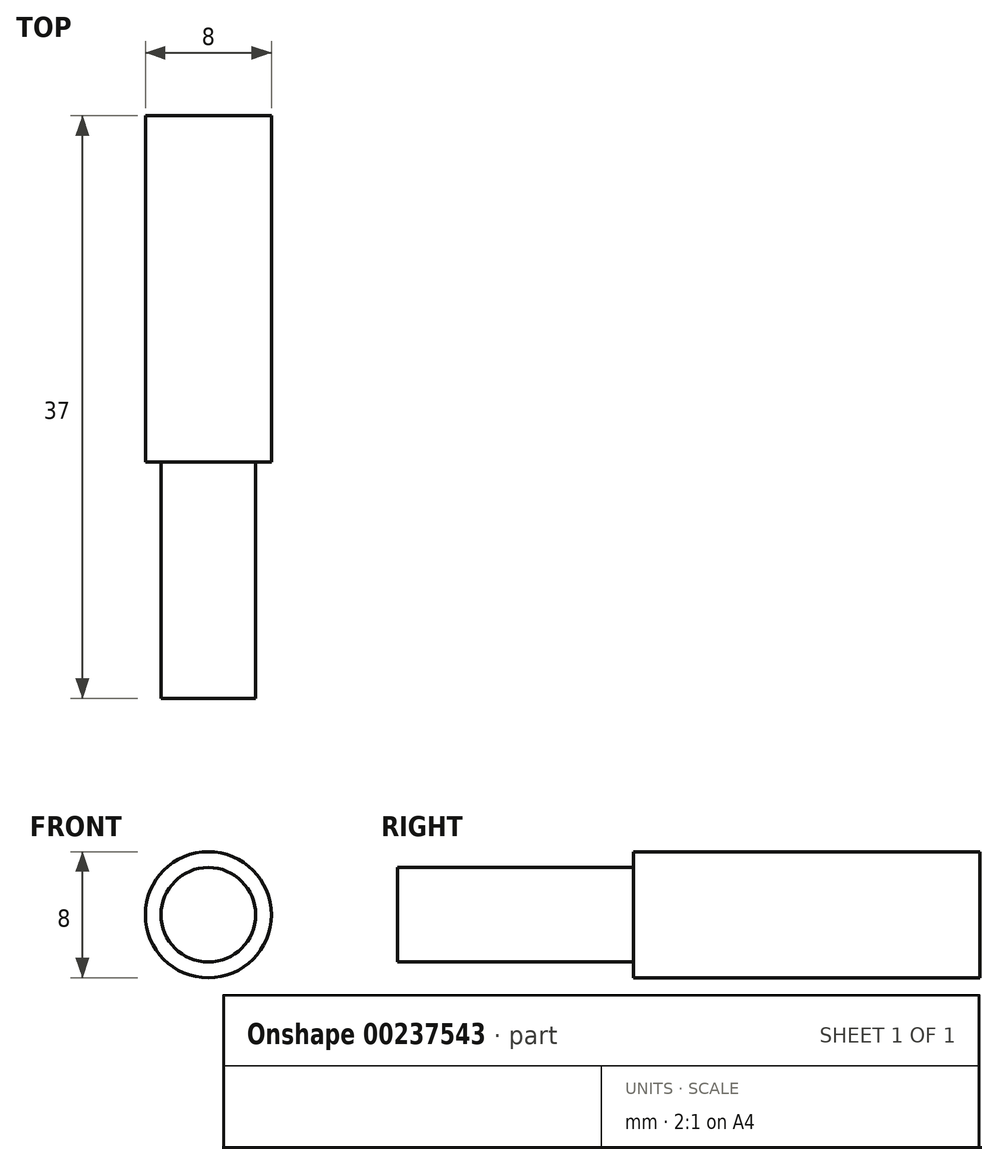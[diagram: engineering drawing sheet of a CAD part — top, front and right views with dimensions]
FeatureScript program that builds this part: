
annotation { "Feature Type Name" : "Feature", "Feature Type Description" : "" }
export const myFeature = defineFeature(function(context is Context, id is Id, definition is map)
    precondition{}
    {
        {
            var Q0;
            Q0=qCreatedBy(makeId("Right.planeOp"),FACE);
            var sketch = newSketch(context, id + "F0", { "sketchPlane" : qUnion([Q0])});
            skLineSegment(sketch, "E0", {"start": v(21.08, 0) * mm, "end": v(-16.68, 0) * mm, "construction": true});
            skLineSegment(sketch, "E1", {"start": v(21.08, 0) * mm, "end": v(21.08, 4) * mm});
            skLineSegment(sketch, "E2", {"start": v(21.08, 4) * mm, "end": v(-0.92, 4) * mm});
            skLineSegment(sketch, "E3", {"start": v(-0.92, 4) * mm, "end": v(-0.92, 3) * mm});
            skLineSegment(sketch, "E4", {"start": v(-0.92, 3) * mm, "end": v(-15.92, 3) * mm});
            skLineSegment(sketch, "E5", {"start": v(-15.92, 3) * mm, "end": v(-15.92, 0) * mm});
            skLineSegment(sketch, "E6", {"start": v(-15.92, 0) * mm, "end": v(21.08, 0) * mm});
            skSolve(sketch);
        }
        {
            var Q0;
            Q0 = qSketchRegion(id + "F0", true);
            var Q1;
            Q1=sQuery(id+"F0.wireOp",EDGE,"E6");
            revolve(context, id + "F1", {"entities" : qUnion([Q0]), "axis" : qUnion([Q1]), "revolveType" : RevolveType.FULL});
        }
    });
